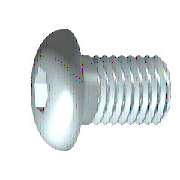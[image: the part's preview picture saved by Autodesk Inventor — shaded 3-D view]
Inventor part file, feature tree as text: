
AUTODESK INVENTOR PART (.ipt)
format: ipt  version: 2015 (Build 190159000, 159)  size: 196,608 bytes
history: native  units: mm (DEFAULTED — no unit token found)
features: sketch x2, extrude x1, plane x1, fillet x1
ambient origin geometry x7: Origin, YZ Plane, XY Plane, X Axis, Y Axis, Z Axis, Center Point
bodies: Solid1 (feature_tree), Body (feature_tree)
feature tree (5):
  extrude  "Slot"  Depth=1.8542mm
  plane  "Work Plane1"
  fillet  "Fillet2"  Radius=1.8542mm
  sketch  "Sketch1"  dims[d1=7.93476mm d2=1.59014mm d3=1.8542mm]
  sketch  "Sketch2"  dims[d4=1.1176mm d5=60.0deg d6=3.5052mm d7=3.5052mm d8=2.287693mm d9=6.6548mm d10=90.0deg d11=10.0mm d12=0.0mm d13=7.93476mm d14=0.0mm d15=0.486918mm d16=0.486918mm d17=1.6002mm d19=0.0mm d26=9.525mm d27=45.0deg d28=0.0mm d29=0.0mm d30=0.1mm]
